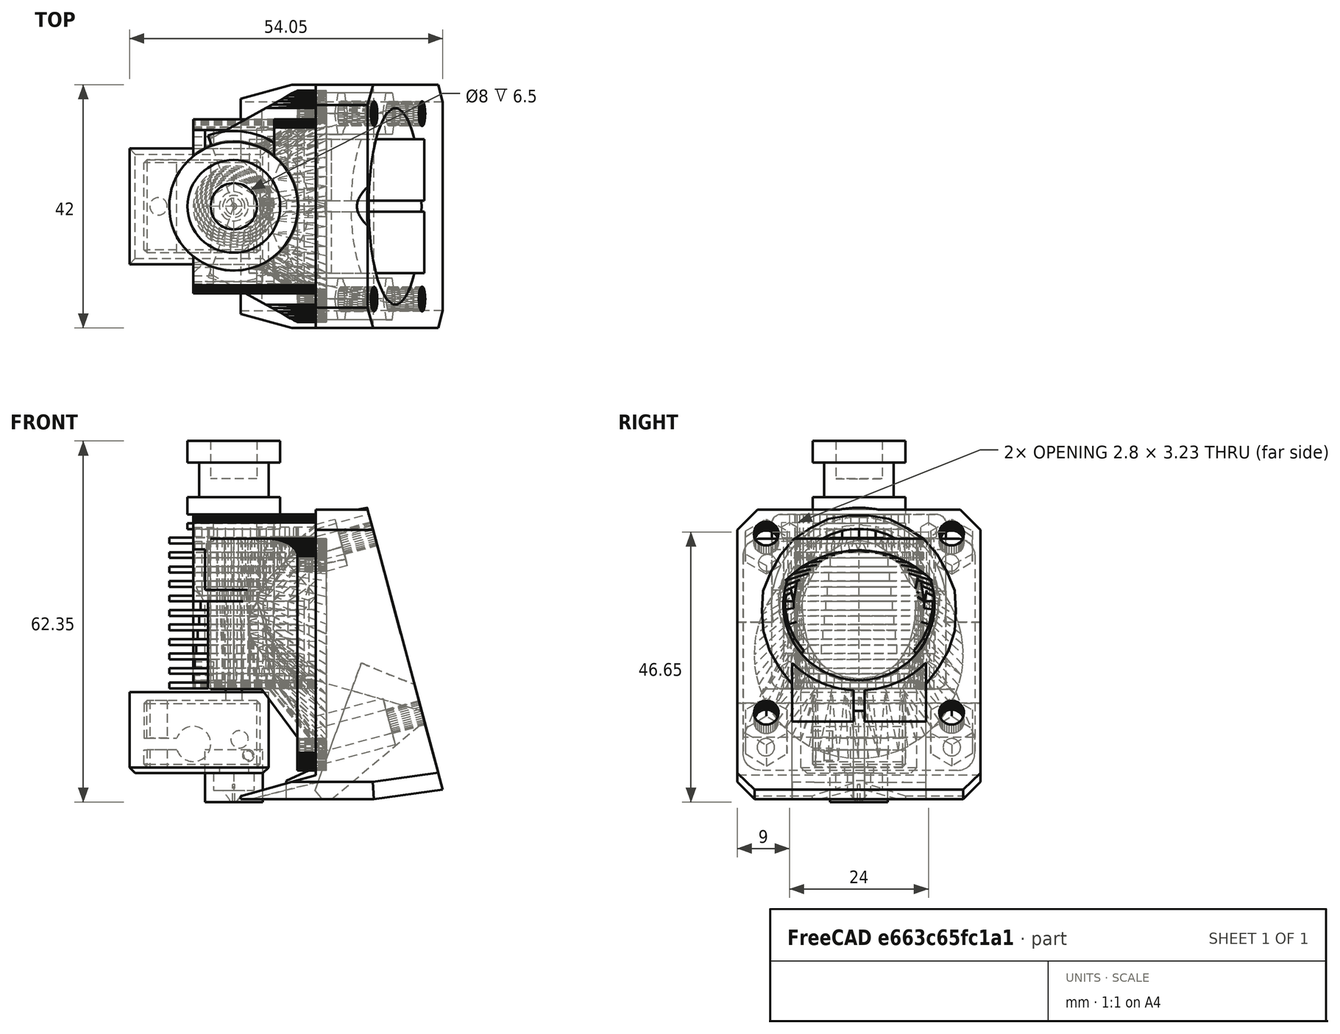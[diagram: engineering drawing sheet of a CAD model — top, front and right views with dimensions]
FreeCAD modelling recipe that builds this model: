
FCSTD DOCUMENT  (FreeCAD 0.15R4061 (Git))
Label: E3Dv6_40mmDuctedShroud
License: CC-BY 3.0
LicenseURL: http://creativecommons.org/licenses/by/3.0/
objects: Part::Feature×7, Part::Box×7, Part::Cut×4, Part::MultiFuse×3, Part::Cylinder×2, Mesh::Feature×2, Part::Cone×2, PartDesign::Draft×2, PartDesign::Chamfer×1, Part::MultiCommon×1
note: 29 computed .brp shape members not serialized (recipe doc carries the construction recipe); baked Part::Feature solids carry a one-line shape summary decoded from their .brp

FEATURE [Part::Feature] Part__Feature  label="E3D V6 1.75mm Universal HotEnd Mockup"
  Placement = pos=(0,0,41) rot=(1,0,0;1.5708rad)
  shape: bbox 26.65 x 22.3 x 62.3 mm, 111 faces (baked)
FEATURE [Part::Cylinder] Cylinder
  Angle = 220
  Height = 26
  Placement = pos=(0,0,19.6) rot=(0,0,-1;1.91986rad)
  Radius = 13
FEATURE [Part::Feature] fanAdapterShort001_solid001  label="fanAdapterShort001 (Solid)001"
  Placement = pos=(16,0,25.5) rot=(0,0,1;3.14159rad)
  shape: bbox 20 x 40 x 40 mm, 716 faces (baked)
FEATURE [Part::Cylinder] Cylinder001
  Angle = 360
  Height = 9
  Radius = 5
FEATURE [Part::Box] Box  label="Cube"
  Height = 14
  Length = 24
  Placement = pos=(-18,-10,5) rot=(0,0,1;0rad)
  Width = 20
FEATURE [PartDesign::Chamfer] Chamfer
  Base = -> Box [Edge4,Edge11,Edge8,Edge9]
  Placement = pos=(-18,-10,5) rot=(0,0,1;0rad)
  Size = 1
FEATURE [Mesh::Feature] DUAL_FAN___LEONOZZLE_V1_1  label="DUAL_FAN_-_LEONOZZLE_V1.1"
  Placement = pos=(31,-4,21.5) rot=(0,-1,0;1.8326rad)
FEATURE [Mesh::Feature] V6_6_Duct  label="V6.6_Duct"
  Placement = pos=(0,0,19.6) rot=(0.002361,0.707105,0.707105;3.14159rad)
FEATURE [Part::Box] Box001  label="Cube001"
  Height = 40
  Length = 30
  Placement = pos=(-15.85,-25,17) rot=(0,0,1;0rad)
  Width = 50
FEATURE [Part::Feature] DUAL_FAN___LEONOZZLE_V1_1001
  shape: bbox 42 x 42 x 50 mm, 2888 faces, 0 solids (baked)
FEATURE [Part::Feature] DUAL_FAN___LEONOZZLE_V1_1001_solid  label="DUAL_FAN___LEONOZZLE_V1_1001 (Solid)"
  shape: bbox 42 x 42 x 50 mm, 2888 faces (baked)
FEATURE [Part::Cone] Cone
  Angle = 360
  Height = 19
  Placement = pos=(14,0,34.1) rot=(0,1,0;1.5708rad)
  Radius1 = 13
  Radius2 = 18.5
FEATURE [Part::Cone] Cone001
  Angle = 360
  Height = 19
  Placement = pos=(13.7,0,34.1) rot=(0,1,0;1.5708rad)
  Radius1 = 15
  Radius2 = 18.5
FEATURE [Part::MultiFuse] Fusion
  Shapes = -> [DUAL_FAN___LEONOZZLE_V1_1001_solid,Cone001]
FEATURE [Part::Box] Box002  label="Cube002"
  Height = 40
  Length = 30
  Placement = pos=(33,-25,14) rot=(0,-1,0;0.261799rad)
  Width = 50
FEATURE [Part::Cut] Cut
  Base = -> Fusion
  Tool = -> Box001
FEATURE [Part::Cut] Cut001
  Base = -> Cut
  Tool = -> Box002
FEATURE [Part::Box] Box004  label="Cube004"
  Height = 35
  Length = 3
  Placement = pos=(14,-11.55,2) rot=(0,1,0;0.872665rad)
  Width = 10.6
FEATURE [PartDesign::Draft] Draft001
  Angle = 30
  Base = -> Box004 [Face1]
  NeutralPlane = -> Box004 [Face5]
  Placement = pos=(14,-11.55,2) rot=(0,1,0;0.872665rad)
  Reversed = true
FEATURE [Part::Box] Box005  label="Cube005"
  Height = 35
  Length = 3
  Placement = pos=(14,1,2) rot=(0,1,0;0.872665rad)
  Width = 10.6
FEATURE [PartDesign::Draft] Draft
  Angle = 30
  Base = -> Box005 [Face1]
  NeutralPlane = -> Box005 [Face5]
  Placement = pos=(14,1,2) rot=(0,1,0;0.872665rad)
  Reversed = true
FEATURE [Part::MultiFuse] Fusion001
  Shapes = -> [Cone,Draft001,Draft]
FEATURE [Part::Cut] Cut002
  Base = -> Cut001
  Tool = -> Fusion001
FEATURE [Part::Feature] Dave_E3Dv6_top002
  Placement = pos=(-15,0,34.65) rot=(1,0,0;3.14159rad)
  shape: bbox 22 x 30 x 30 mm, 476 faces, 0 solids (baked)
FEATURE [Part::Box] Box006  label="Cube006"
  Height = 80
  Length = 10
  Placement = pos=(36.9,-29,-1) rot=(0,-1,0;0.261799rad)
  Width = 66
FEATURE [Part::Cut] Cut003
  Base = -> Cut002
  Tool = -> Box006
FEATURE [Part::Feature] Cut004
  shape: bbox 34.88 x 42 x 51.93 mm, 559 faces (baked)
FEATURE [Part::Box] Box007  label="Cube007"
  Height = 40
  Length = 30
  Placement = pos=(-15.85,-25,17) rot=(0,0,1;0rad)
  Width = 50
FEATURE [Part::Feature] Dave_E3Dv6_bottom002_solid  label="Dave_E3Dv6_bottom002 (Solid)"
  shape: bbox 22 x 30 x 30 mm, 467 faces (baked)
FEATURE [Part::MultiCommon] Common
  Shapes = -> [Dave_E3Dv6_bottom002_solid,Box007]
FEATURE [Part::MultiFuse] Fusion002
  Shapes = -> [Cut003,Common]
